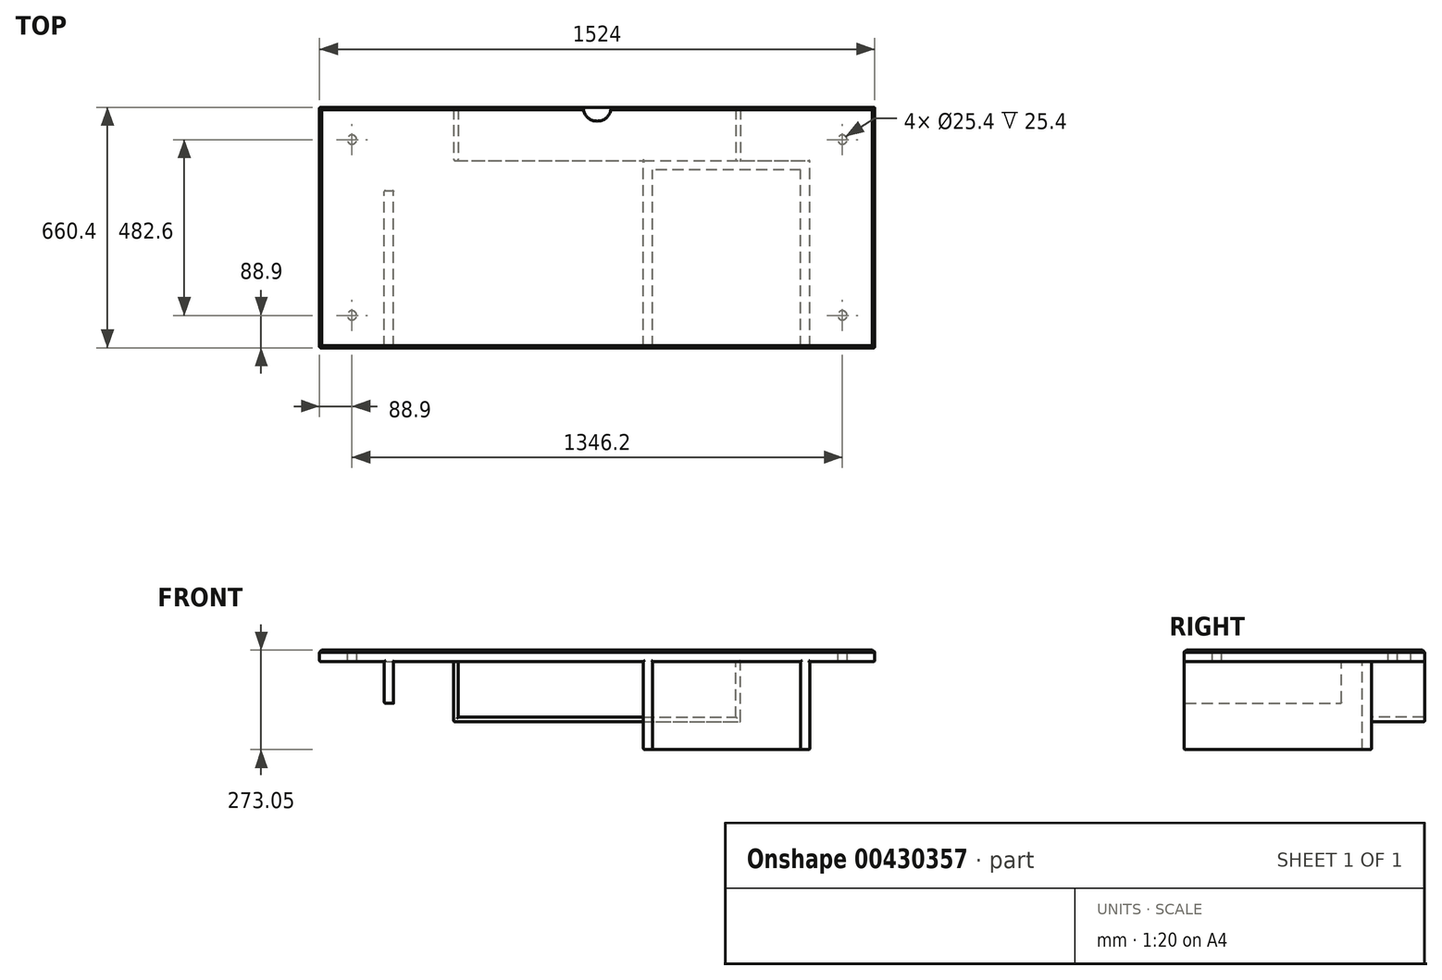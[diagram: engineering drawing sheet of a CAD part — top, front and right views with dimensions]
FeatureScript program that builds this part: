
annotation { "Feature Type Name" : "Feature", "Feature Type Description" : "" }
export const myFeature = defineFeature(function(context is Context, id is Id, definition is map)
    precondition{}
    {
        {
            var Q0;
            Q0=qCreatedBy(makeId("Top.planeOp"),FACE);
            var sketch = newSketch(context, id + "F0", { "sketchPlane" : qUnion([Q0])});
            skLineSegment(sketch, "E0.bottom", {"start": v(-762, 330.2) * mm, "end": v(762, 330.2) * mm});
            skLineSegment(sketch, "E0.top", {"start": v(-762, -330.2) * mm, "end": v(762, -330.2) * mm});
            skLineSegment(sketch, "E0.left", {"start": v(-762, 330.2) * mm, "end": v(-762, -330.2) * mm});
            skLineSegment(sketch, "E0.right", {"start": v(762, 330.2) * mm, "end": v(762, -330.2) * mm});
            skPoint(sketch, "E0.middle", {"position": v(0, 0) * mm});
            skSolve(sketch);
        }
        {
            var Q0;
            Q0=qSketchRegion(id+"F0",true);
            extrude(context, id + "F1", {"entities" : qUnion([Q0]), "oppositeDirection" : true, "depth" : 31.75 * mm});
        }
        {
            var Q0;
            Q0=makeQuery(id+"F1.opExtrude","CAP_FACE",FACE,{"disambiguationData":[OSD([sQuery(id+"F0.wireOp",EDGE,"E0.bottom"),sQuery(id+"F0.wireOp",EDGE,"E0.top"),sQuery(id+"F0.wireOp",EDGE,"E0.left"),sQuery(id+"F0.wireOp",EDGE,"E0.right")])],"isStart":true});
            var sketch = newSketch(context, id + "F2", { "sketchPlane" : qUnion([Q0])});
            skCircle(sketch, "E1", {"center": v(0, 330.2) * mm, "radius": 38.1 * mm});
            skSolve(sketch);
        }
        {
            var Q0;
            Q0=qSketchRegion(id+"F2",true);
            extrude(context, id + "F3", {"entities" : qUnion([Q0]), "operationType" : NewBodyOperationType.REMOVE, "endBound" : BoundingType.THROUGH_ALL, "oppositeDirection" : true, "depth" : 25.4 * mm});
        }
        {
            var Q0;
            Q0=makeQuery(id+"F1.opExtrude","CAP_FACE",FACE,{"disambiguationData":[OSD([sQuery(id+"F0.wireOp",EDGE,"E0.bottom"),sQuery(id+"F0.wireOp",EDGE,"E0.top"),sQuery(id+"F0.wireOp",EDGE,"E0.left"),sQuery(id+"F0.wireOp",EDGE,"E0.right")])],"isStart":false});
            var sketch = newSketch(context, id + "F4", { "sketchPlane" : qUnion([Q0])});
            skLineSegment(sketch, "E2.bottom", {"start": v(-584.2, 330.2) * mm, "end": v(-558.8, 330.2) * mm});
            skLineSegment(sketch, "E2.top", {"start": v(-584.2, -101.6) * mm, "end": v(-558.8, -101.6) * mm});
            skLineSegment(sketch, "E2.left", {"start": v(-584.2, 330.2) * mm, "end": v(-584.2, -101.6) * mm});
            skLineSegment(sketch, "E2.right", {"start": v(-558.8, 330.2) * mm, "end": v(-558.8, -101.6) * mm});
            skPoint(sketch, "E3.oppositeSnap0", {"position": v(-571.5, -101.6) * mm});
            skSolve(sketch);
        }
        {
            var Q0;
            Q0=qSketchRegion(id+"F4",true);
            extrude(context, id + "F5", {"entities" : qUnion([Q0]), "operationType" : NewBodyOperationType.ADD, "depth" : 114.3 * mm});
        }
        {
            var Q0;
            {var subQ0=sQuery(id+"F0.wireOp",EDGE,"E0.bottom");var subQ1=sQuery(id+"F0.wireOp",EDGE,"E0.right");Q0=makeQuery(id+"F3.boolean.opBoolean","SPLIT",EDGE,{"disambiguationData":[TD([makeQuery(id+"F1.opExtrude","SWEPT_FACE",FACE,{"disambiguationData":[OSD([subQ1])]})])],"derivedFrom":makeQuery(id+"F1.opExtrude","CAP_EDGE",EDGE,{"disambiguationData":[OSD([subQ0])],"isStart":true})});}
            var Q1;
            Q1=makeQuery(id+"F1.opExtrude","CAP_EDGE",EDGE,{"disambiguationData":[OSD([sQuery(id+"F0.wireOp",EDGE,"E0.right")])],"isStart":true});
            var Q2;
            {var subQ0=sQuery(id+"F0.wireOp",EDGE,"E0.bottom");var subQ1=sQuery(id+"F0.wireOp",EDGE,"E0.left");Q2=makeQuery(id+"F3.boolean.opBoolean","SPLIT",EDGE,{"disambiguationData":[TD([makeQuery(id+"F1.opExtrude","SWEPT_FACE",FACE,{"disambiguationData":[OSD([subQ1])]})])],"derivedFrom":makeQuery(id+"F1.opExtrude","CAP_EDGE",EDGE,{"disambiguationData":[OSD([subQ0])],"isStart":true})});}
            var Q3;
            Q3=makeQuery(id+"F1.opExtrude","CAP_EDGE",EDGE,{"disambiguationData":[OSD([sQuery(id+"F0.wireOp",EDGE,"E0.left")])],"isStart":true});
            var Q4;
            Q4=makeQuery(id+"F1.opExtrude","CAP_EDGE",EDGE,{"disambiguationData":[OSD([sQuery(id+"F0.wireOp",EDGE,"E0.top")])],"isStart":true});
            var Q5;
            Q5=makeQuery(id+"F3.boolean.opBoolean","COPY",EDGE,{"derivedFrom":makeQuery(id+"F3.opExtrude","CAP_EDGE",EDGE,{"disambiguationData":[OSD([sQuery(id+"F2.wireOp",EDGE,"E1")])],"isStart":true})});
            chamfer(context, id + "F6", {"entities" : qUnion([Q0, Q1, Q2, Q3, Q4, Q5]), "width" : 6.35 * mm, "tangentPropagation" : true});
        }
        {
            var Q0;
            Q0=makeQuery(id+"F1.opExtrude","CAP_FACE",FACE,{"disambiguationData":[OSD([sQuery(id+"F0.wireOp",EDGE,"E0.bottom"),sQuery(id+"F0.wireOp",EDGE,"E0.top"),sQuery(id+"F0.wireOp",EDGE,"E0.left"),sQuery(id+"F0.wireOp",EDGE,"E0.right")])],"isStart":false});
            var sketch = newSketch(context, id + "F7", { "sketchPlane" : qUnion([Q0])});
            skCircle(sketch, "E4", {"center": v(-673.1, 241.3) * mm, "radius": 12.7 * mm});
            skCircle(sketch, "E5", {"center": v(-673.1, -241.3) * mm, "radius": 12.7 * mm});
            skCircle(sketch, "E6", {"center": v(673.1, 241.3) * mm, "radius": 12.7 * mm});
            skCircle(sketch, "E7", {"center": v(673.1, -241.3) * mm, "radius": 12.7 * mm});
            skSolve(sketch);
        }
        {
            var Q0;
            Q0=qSketchRegion(id+"F7",true);
            extrude(context, id + "F8", {"entities" : qUnion([Q0]), "operationType" : NewBodyOperationType.REMOVE, "oppositeDirection" : true, "depth" : 25.4 * mm});
        }
        {
            var Q0;
            Q0=makeQuery(id+"F1.opExtrude","CAP_FACE",FACE,{"disambiguationData":[OSD([sQuery(id+"F0.wireOp",EDGE,"E0.bottom"),sQuery(id+"F0.wireOp",EDGE,"E0.top"),sQuery(id+"F0.wireOp",EDGE,"E0.left"),sQuery(id+"F0.wireOp",EDGE,"E0.right")])],"isStart":false});
            var sketch = newSketch(context, id + "F9", { "sketchPlane" : qUnion([Q0])});
            skLineSegment(sketch, "E8.bottom", {"start": v(127, 330.2) * mm, "end": v(152.4, 330.2) * mm});
            skLineSegment(sketch, "E8.top", {"start": v(127, -184.15) * mm, "end": v(152.4, -184.15) * mm});
            skLineSegment(sketch, "E8.left", {"start": v(127, 330.2) * mm, "end": v(127, -184.15) * mm});
            skLineSegment(sketch, "E8.right", {"start": v(152.4, 330.2) * mm, "end": v(152.4, -158.75) * mm});
            skLineSegment(sketch, "E9.bottom", {"start": v(558.8, 330.2) * mm, "end": v(584.2, 330.2) * mm});
            skLineSegment(sketch, "E9.top", {"start": v(558.8, -184.15) * mm, "end": v(584.2, -184.15) * mm});
            skLineSegment(sketch, "E9.left", {"start": v(558.8, 330.2) * mm, "end": v(558.8, -158.75) * mm});
            skLineSegment(sketch, "E9.right", {"start": v(584.2, 330.2) * mm, "end": v(584.2, -184.15) * mm});
            skLineSegment(sketch, "E10", {"start": v(584.2, -184.15) * mm, "end": v(127, -184.15) * mm});
            skLineSegment(sketch, "E11", {"start": v(558.8, -158.75) * mm, "end": v(152.4, -158.75) * mm});
            skSolve(sketch);
        }
        {
            var Q0;
            Q0=qSketchRegion(id+"F9",true);
            extrude(context, id + "F10", {"entities" : qUnion([Q0]), "operationType" : NewBodyOperationType.ADD, "depth" : 241.3 * mm});
        }
        {
            var Q0;
            {var subQ0=sQuery(id+"F0.wireOp",EDGE,"E0.bottom");var subQ1=sQuery(id+"F0.wireOp",EDGE,"E0.right");var subQ2=sQuery(id+"F0.wireOp",EDGE,"E0.top");var subQ3=sQuery(id+"F0.wireOp",EDGE,"E0.left");Q0=makeQuery(id+"F10.boolean.opBoolean","SPLIT",FACE,{"disambiguationData":[TD([makeQuery(id+"F1.opExtrude","SWEPT_FACE",FACE,{"disambiguationData":[OSD([subQ0])]})])],"derivedFrom":makeQuery(id+"F1.opExtrude","CAP_FACE",FACE,{"disambiguationData":[OSD([subQ0,subQ2,subQ3,subQ1])],"isStart":false})});}
            var sketch = newSketch(context, id + "F11", { "sketchPlane" : qUnion([Q0])});
            skLineSegment(sketch, "E12.bottom", {"start": v(-393.7, -330.2) * mm, "end": v(-381, -330.2) * mm});
            skLineSegment(sketch, "E12.top", {"start": v(-393.7, -184.15) * mm, "end": v(-381, -184.15) * mm});
            skLineSegment(sketch, "E12.left", {"start": v(-393.7, -330.2) * mm, "end": v(-393.7, -184.15) * mm});
            skLineSegment(sketch, "E12.right", {"start": v(-381, -330.2) * mm, "end": v(-381, -184.15) * mm});
            skLineSegment(sketch, "E13.bottom", {"start": v(393.7, -330.2) * mm, "end": v(381, -330.2) * mm});
            skLineSegment(sketch, "E13.top", {"start": v(393.7, -184.15) * mm, "end": v(381, -184.15) * mm});
            skLineSegment(sketch, "E13.left", {"start": v(393.7, -330.2) * mm, "end": v(393.7, -184.15) * mm});
            skLineSegment(sketch, "E13.right", {"start": v(381, -330.2) * mm, "end": v(381, -184.15) * mm});
            skLineSegment(sketch, "E14", {"start": v(-381, -330.2) * mm, "end": v(0, -330.2) * mm, "construction": true});
            skLineSegment(sketch, "E15", {"start": v(0, -330.2) * mm, "end": v(381, -330.2) * mm, "construction": true});
            skSolve(sketch);
        }
        {
            var Q0;
            Q0 = qSketchRegion(id + "F11", true);
            extrude(context, id + "F12", {"entities" : qUnion([Q0]), "operationType" : NewBodyOperationType.ADD, "depth" : 152.4 * mm});
        }
        {
            var Q0;
            Q0=makeQuery(id+"F12.opExtrude","CAP_FACE",FACE,{"disambiguationData":[OSD([sQuery(id+"F11.wireOp",EDGE,"E12.bottom"),sQuery(id+"F11.wireOp",EDGE,"E12.top"),sQuery(id+"F11.wireOp",EDGE,"E12.left"),sQuery(id+"F11.wireOp",EDGE,"E12.right")])],"isStart":false});
            var sketch = newSketch(context, id + "F13", { "sketchPlane" : qUnion([Q0])});
            skLineSegment(sketch, "E16.bottom", {"start": v(-393.7, -184.15) * mm, "end": v(393.7, -184.15) * mm});
            skLineSegment(sketch, "E16.top", {"start": v(-393.7, -330.2) * mm, "end": v(393.7, -330.2) * mm});
            skLineSegment(sketch, "E16.left", {"start": v(-393.7, -184.15) * mm, "end": v(-393.7, -330.2) * mm});
            skLineSegment(sketch, "E16.right", {"start": v(393.7, -184.15) * mm, "end": v(393.7, -330.2) * mm});
            skSolve(sketch);
        }
        {
            var Q0;
            Q0 = qSketchRegion(id + "F13", true);
            extrude(context, id + "F14", {"entities" : qUnion([Q0]), "operationType" : NewBodyOperationType.ADD, "depth" : 12.7 * mm});
        }
        {
            var Q0;
            {var subQ0=sQuery(id+"F0.wireOp",EDGE,"E0.left");var subQ1=sQuery(id+"F0.wireOp",EDGE,"E0.top");Q0=makeQuery(id+"F5.boolean.opBoolean","SPLIT",EDGE,{"disambiguationData":[TD([makeQuery(id+"F1.opExtrude","SWEPT_FACE",FACE,{"disambiguationData":[OSD([subQ0])]})])],"derivedFrom":makeQuery(id+"F1.opExtrude","CAP_EDGE",EDGE,{"disambiguationData":[OSD([subQ1])],"isStart":false})});}
            var Q1;
            {var subQ0=sQuery(id+"F0.wireOp",EDGE,"E0.bottom");var subQ1=sQuery(id+"F0.wireOp",EDGE,"E0.right");Q1=makeQuery(id+"F3.boolean.opBoolean","SPLIT",EDGE,{"disambiguationData":[TD([makeQuery(id+"F1.opExtrude","SWEPT_FACE",FACE,{"disambiguationData":[OSD([subQ1])]})])],"derivedFrom":makeQuery(id+"F1.opExtrude","CAP_EDGE",EDGE,{"disambiguationData":[OSD([subQ0])],"isStart":false})});}
            var Q2;
            {var subQ0=sQuery(id+"F0.wireOp",EDGE,"E0.bottom");var subQ1=sQuery(id+"F0.wireOp",EDGE,"E0.left");Q2=makeQuery(id+"F3.boolean.opBoolean","SPLIT",EDGE,{"disambiguationData":[TD([makeQuery(id+"F1.opExtrude","SWEPT_FACE",FACE,{"disambiguationData":[OSD([subQ1])]})])],"derivedFrom":makeQuery(id+"F1.opExtrude","CAP_EDGE",EDGE,{"disambiguationData":[OSD([subQ0])],"isStart":false})});}
            var Q3;
            Q3=makeQuery(id+"F1.opExtrude","CAP_EDGE",EDGE,{"disambiguationData":[OSD([sQuery(id+"F0.wireOp",EDGE,"E0.left")])],"isStart":false});
            var Q4;
            Q4=makeQuery(id+"F1.opExtrude","CAP_EDGE",EDGE,{"disambiguationData":[OSD([sQuery(id+"F0.wireOp",EDGE,"E0.right")])],"isStart":false});
            var Q5;
            Q5=makeQuery(id+"F5.opExtrude","SWEPT_EDGE",EDGE,{"disambiguationData":[OSD([sQuery(id+"F0.wireOp",EDGE,"E0.top"),sQuery(id+"F4.wireOp",EDGE,"E2.bottom"),sQuery(id+"F4.wireOp",EDGE,"E2.left")])]});
            var Q6;
            Q6=makeQuery(id+"F5.opExtrude","SWEPT_EDGE",EDGE,{"disambiguationData":[OSD([sQuery(id+"F0.wireOp",EDGE,"E0.top"),sQuery(id+"F4.wireOp",EDGE,"E2.bottom"),sQuery(id+"F4.wireOp",EDGE,"E2.right")])]});
            var Q7;
            Q7=makeQuery(id+"F5.opExtrude","CAP_EDGE",EDGE,{"disambiguationData":[OSD([sQuery(id+"F4.wireOp",EDGE,"E2.bottom")])],"isStart":false});
            var Q8;
            Q8=makeQuery(id+"F5.opExtrude","SWEPT_EDGE",EDGE,{"disambiguationData":[OSD([sQuery(id+"F0.wireOp",EDGE,"E0.top"),sQuery(id+"F4.wireOp",EDGE,"E2.bottom"),sQuery(id+"F4.wireOp",EDGE,"E2.left")])]});
            var Q9;
            Q9=makeQuery(id+"F5.opExtrude","SWEPT_EDGE",EDGE,{"disambiguationData":[OSD([sQuery(id+"F0.wireOp",EDGE,"E0.top"),sQuery(id+"F4.wireOp",EDGE,"E2.bottom"),sQuery(id+"F4.wireOp",EDGE,"E2.right")])]});
            var Q10;
            Q10=makeQuery(id+"F5.opExtrude","SWEPT_EDGE",EDGE,{"disambiguationData":[OSD([sQuery(id+"F0.wireOp",EDGE,"E0.top"),sQuery(id+"F4.wireOp",EDGE,"E2.bottom"),sQuery(id+"F4.wireOp",EDGE,"E2.left")])]});
            var Q11;
            Q11=makeQuery(id+"F5.opExtrude","SWEPT_EDGE",EDGE,{"disambiguationData":[OSD([sQuery(id+"F0.wireOp",EDGE,"E0.top"),sQuery(id+"F4.wireOp",EDGE,"E2.bottom"),sQuery(id+"F4.wireOp",EDGE,"E2.right")])]});
            var Q12;
            Q12=makeQuery(id+"F5.opExtrude","SWEPT_EDGE",EDGE,{"disambiguationData":[OSD([sQuery(id+"F4.wireOp",EDGE,"E2.top"),sQuery(id+"F4.wireOp",EDGE,"E2.left")])]});
            var Q13;
            Q13=makeQuery(id+"F5.opExtrude","SWEPT_EDGE",EDGE,{"disambiguationData":[OSD([sQuery(id+"F4.wireOp",EDGE,"E2.top"),sQuery(id+"F4.wireOp",EDGE,"E2.right")])]});
            var Q14;
            Q14=makeQuery(id+"F5.opExtrude","CAP_EDGE",EDGE,{"disambiguationData":[OSD([sQuery(id+"F4.wireOp",EDGE,"E2.top")])],"isStart":false});
            var Q15;
            Q15=makeQuery(id+"F5.opExtrude","CAP_EDGE",EDGE,{"disambiguationData":[OSD([sQuery(id+"F4.wireOp",EDGE,"E2.left")])],"isStart":false});
            var Q16;
            {var subQ0=sQuery(id+"F0.wireOp",EDGE,"E0.top");var subQ2=makeQuery(id+"F5.opExtrude","SWEPT_FACE",FACE,{"disambiguationData":[OSD([sQuery(id+"F4.wireOp",EDGE,"E2.right")])]});var subQ4=sQuery(id+"F0.wireOp",EDGE,"E0.right");Q16=makeQuery(id+"F10.boolean.opBoolean","SPLIT",EDGE,{"disambiguationData":[TD([subQ2])],"derivedFrom":makeQuery(id+"F5.boolean.opBoolean","SPLIT",EDGE,{"disambiguationData":[TD([makeQuery(id+"F1.opExtrude","SWEPT_FACE",FACE,{"disambiguationData":[OSD([subQ4])]})])],"derivedFrom":makeQuery(id+"F1.opExtrude","CAP_EDGE",EDGE,{"disambiguationData":[OSD([subQ0])],"isStart":false})})});}
            var Q17;
            Q17=makeQuery(id+"F10.opExtrude","SWEPT_EDGE",EDGE,{"disambiguationData":[OSD([sQuery(id+"F0.wireOp",EDGE,"E0.top"),sQuery(id+"F9.wireOp",EDGE,"E8.bottom"),sQuery(id+"F9.wireOp",EDGE,"E8.left")])]});
            var Q18;
            Q18=makeQuery(id+"F10.opExtrude","SWEPT_EDGE",EDGE,{"disambiguationData":[OSD([sQuery(id+"F0.wireOp",EDGE,"E0.top"),sQuery(id+"F9.wireOp",EDGE,"E8.bottom"),sQuery(id+"F9.wireOp",EDGE,"E8.right")])]});
            var Q19;
            {var subQ0=sQuery(id+"F0.wireOp",EDGE,"E0.top");var subQ3=sQuery(id+"F0.wireOp",EDGE,"E0.right");Q19=makeQuery(id+"F10.boolean.opBoolean","SPLIT",EDGE,{"disambiguationData":[TD([makeQuery(id+"F10.opExtrude","SWEPT_FACE",FACE,{"disambiguationData":[OSD([sQuery(id+"F9.wireOp",EDGE,"E8.right")])]})])],"derivedFrom":makeQuery(id+"F5.boolean.opBoolean","SPLIT",EDGE,{"disambiguationData":[TD([makeQuery(id+"F1.opExtrude","SWEPT_FACE",FACE,{"disambiguationData":[OSD([subQ3])]})])],"derivedFrom":makeQuery(id+"F1.opExtrude","CAP_EDGE",EDGE,{"disambiguationData":[OSD([subQ0])],"isStart":false})})});}
            var Q20;
            Q20=makeQuery(id+"F10.opExtrude","SWEPT_EDGE",EDGE,{"disambiguationData":[OSD([sQuery(id+"F0.wireOp",EDGE,"E0.top"),sQuery(id+"F9.wireOp",EDGE,"E9.bottom"),sQuery(id+"F9.wireOp",EDGE,"E9.left")])]});
            var Q21;
            Q21=makeQuery(id+"F10.opExtrude","SWEPT_EDGE",EDGE,{"disambiguationData":[OSD([sQuery(id+"F0.wireOp",EDGE,"E0.top"),sQuery(id+"F9.wireOp",EDGE,"E9.bottom"),sQuery(id+"F9.wireOp",EDGE,"E9.right")])]});
            var Q22;
            {var subQ0=sQuery(id+"F0.wireOp",EDGE,"E0.right");var subQ1=makeQuery(id+"F1.opExtrude","SWEPT_FACE",FACE,{"disambiguationData":[OSD([subQ0])]});var subQ2=sQuery(id+"F0.wireOp",EDGE,"E0.top");Q22=makeQuery(id+"F10.boolean.opBoolean","SPLIT",EDGE,{"disambiguationData":[TD([subQ1])],"derivedFrom":makeQuery(id+"F5.boolean.opBoolean","SPLIT",EDGE,{"disambiguationData":[TD([subQ1])],"derivedFrom":makeQuery(id+"F1.opExtrude","CAP_EDGE",EDGE,{"disambiguationData":[OSD([subQ2])],"isStart":false})})});}
            var Q23;
            Q23=makeQuery(id+"F1.opExtrude","SWEPT_EDGE",EDGE,{"disambiguationData":[OSD([sQuery(id+"F0.wireOp",EDGE,"E0.top"),sQuery(id+"F0.wireOp",EDGE,"E0.right")])]});
            var Q24;
            Q24=makeQuery(id+"F10.opExtrude","CAP_EDGE",EDGE,{"disambiguationData":[OSD([sQuery(id+"F9.wireOp",EDGE,"E8.bottom")])],"isStart":false});
            var Q25;
            Q25=makeQuery(id+"F10.opExtrude","CAP_EDGE",EDGE,{"disambiguationData":[OSD([sQuery(id+"F9.wireOp",EDGE,"E9.bottom")])],"isStart":false});
            var Q26;
            Q26=makeQuery(id+"F10.opExtrude","CAP_EDGE",EDGE,{"disambiguationData":[OSD([sQuery(id+"F9.wireOp",EDGE,"E9.right")])],"isStart":false});
            var Q27;
            Q27=makeQuery(id+"F10.opExtrude","CAP_EDGE",EDGE,{"disambiguationData":[OSD([sQuery(id+"F9.wireOp",EDGE,"E8.left")])],"isStart":false});
            var Q28;
            Q28=makeQuery(id+"F10.opExtrude","SWEPT_EDGE",EDGE,{"disambiguationData":[OSD([sQuery(id+"F9.wireOp",EDGE,"E9.right"),sQuery(id+"F9.wireOp",EDGE,"E10")])]});
            var Q29;
            Q29=makeQuery(id+"F10.opExtrude","CAP_EDGE",EDGE,{"disambiguationData":[OSD([sQuery(id+"F9.wireOp",EDGE,"E10")])],"isStart":false});
            var Q30;
            Q30=makeQuery(id+"F1.opExtrude","SWEPT_EDGE",EDGE,{"disambiguationData":[OSD([sQuery(id+"F0.wireOp",EDGE,"E0.bottom"),sQuery(id+"F0.wireOp",EDGE,"E0.right")])]});
            var Q31;
            Q31=makeQuery(id+"F14.boolean.opBoolean","MERGE",EDGE,{"derivedFrom":[makeQuery(id+"F12.opExtrude","SWEPT_EDGE",EDGE,{"disambiguationData":[OSD([sQuery(id+"F0.wireOp",EDGE,"E0.bottom"),sQuery(id+"F11.wireOp",EDGE,"E13.bottom"),sQuery(id+"F11.wireOp",EDGE,"E13.left")])]}),makeQuery(id+"F14.opExtrude","SWEPT_EDGE",EDGE,{"disambiguationData":[OSD([sQuery(id+"F13.wireOp",EDGE,"E16.top"),sQuery(id+"F13.wireOp",EDGE,"E16.right")])]})]});
            var Q32;
            Q32=makeQuery(id+"F12.opExtrude","SWEPT_EDGE",EDGE,{"disambiguationData":[OSD([sQuery(id+"F0.wireOp",EDGE,"E0.bottom"),sQuery(id+"F11.wireOp",EDGE,"E13.bottom"),sQuery(id+"F11.wireOp",EDGE,"E13.right")])]});
            var Q33;
            Q33=makeQuery(id+"F14.opExtrude","CAP_EDGE",EDGE,{"disambiguationData":[OSD([sQuery(id+"F13.wireOp",EDGE,"E16.top")])],"isStart":true});
            var Q34;
            Q34=makeQuery(id+"F14.opExtrude","CAP_EDGE",EDGE,{"disambiguationData":[OSD([sQuery(id+"F13.wireOp",EDGE,"E16.top")])],"isStart":false});
            var Q35;
            Q35=makeQuery(id+"F12.opExtrude","SWEPT_EDGE",EDGE,{"disambiguationData":[OSD([sQuery(id+"F0.wireOp",EDGE,"E0.bottom"),sQuery(id+"F11.wireOp",EDGE,"E12.bottom"),sQuery(id+"F11.wireOp",EDGE,"E12.right")])]});
            var Q36;
            Q36=makeQuery(id+"F14.boolean.opBoolean","MERGE",EDGE,{"derivedFrom":[makeQuery(id+"F12.opExtrude","SWEPT_EDGE",EDGE,{"disambiguationData":[OSD([sQuery(id+"F0.wireOp",EDGE,"E0.bottom"),sQuery(id+"F11.wireOp",EDGE,"E12.bottom"),sQuery(id+"F11.wireOp",EDGE,"E12.left")])]}),makeQuery(id+"F14.opExtrude","SWEPT_EDGE",EDGE,{"disambiguationData":[OSD([sQuery(id+"F13.wireOp",EDGE,"E16.top"),sQuery(id+"F13.wireOp",EDGE,"E16.left")])]})]});
            var Q37;
            Q37=makeQuery(id+"F14.opExtrude","CAP_EDGE",EDGE,{"disambiguationData":[OSD([sQuery(id+"F13.wireOp",EDGE,"E16.left")])],"isStart":false});
            var Q38;
            Q38=makeQuery(id+"F14.opExtrude","CAP_EDGE",EDGE,{"disambiguationData":[OSD([sQuery(id+"F13.wireOp",EDGE,"E16.right")])],"isStart":false});
            var Q39;
            Q39=makeQuery(id+"F12.opExtrude","SWEPT_EDGE",EDGE,{"disambiguationData":[OSD([sQuery(id+"F11.wireOp",EDGE,"E12.top"),sQuery(id+"F11.wireOp",EDGE,"E12.right")])]});
            var Q40;
            Q40=makeQuery(id+"F14.boolean.opBoolean","MERGE",EDGE,{"derivedFrom":[makeQuery(id+"F12.opExtrude","SWEPT_EDGE",EDGE,{"disambiguationData":[OSD([sQuery(id+"F11.wireOp",EDGE,"E12.top"),sQuery(id+"F11.wireOp",EDGE,"E12.left")])]}),makeQuery(id+"F14.opExtrude","SWEPT_EDGE",EDGE,{"disambiguationData":[OSD([sQuery(id+"F13.wireOp",EDGE,"E16.bottom"),sQuery(id+"F13.wireOp",EDGE,"E16.left")])]})]});
            var Q41;
            {var subQ0=sQuery(id+"F13.wireOp",EDGE,"E16.bottom");Q41=makeQuery(id+"F14.boolean.opBoolean","SPLIT",EDGE,{"disambiguationData":[topologyDisambiguationEdgeConnected([makeQuery(id+"F12.opExtrude","SWEPT_FACE",FACE,{"disambiguationData":[OSD([sQuery(id+"F11.wireOp",EDGE,"E12.top")])]})])],"derivedFrom":makeQuery(id+"F14.opExtrude","CAP_EDGE",EDGE,{"disambiguationData":[OSD([subQ0])],"isStart":true})});}
            var Q42;
            {var subQ0=sQuery(id+"F13.wireOp",EDGE,"E16.bottom");Q42=makeQuery(id+"F14.boolean.opBoolean","SPLIT",EDGE,{"disambiguationData":[topologyDisambiguationEdgeConnected([makeQuery(id+"F12.opExtrude","SWEPT_FACE",FACE,{"disambiguationData":[OSD([sQuery(id+"F11.wireOp",EDGE,"E12.top")])]})])],"derivedFrom":makeQuery(id+"F14.opExtrude","CAP_EDGE",EDGE,{"disambiguationData":[OSD([subQ0])],"isStart":false})});}
            var Q43;
            Q43=makeQuery(id+"F1.opExtrude","SWEPT_EDGE",EDGE,{"disambiguationData":[OSD([sQuery(id+"F0.wireOp",EDGE,"E0.bottom"),sQuery(id+"F0.wireOp",EDGE,"E0.left")])]});
            var Q44;
            Q44=makeQuery(id+"F1.opExtrude","SWEPT_EDGE",EDGE,{"disambiguationData":[OSD([sQuery(id+"F0.wireOp",EDGE,"E0.top"),sQuery(id+"F0.wireOp",EDGE,"E0.left")])]});
            var Q45;
            Q45=makeQuery(id+"F3.boolean.opBoolean","INTERSECT",EDGE,{"derivedFrom":[makeQuery(id+"F1.opExtrude","CAP_FACE",FACE,{"disambiguationData":[OSD([sQuery(id+"F0.wireOp",EDGE,"E0.bottom"),sQuery(id+"F0.wireOp",EDGE,"E0.top"),sQuery(id+"F0.wireOp",EDGE,"E0.left"),sQuery(id+"F0.wireOp",EDGE,"E0.right")])],"isStart":false}),makeQuery(id+"F3.opExtrude","SWEPT_FACE",FACE,{"disambiguationData":[OSD([sQuery(id+"F2.wireOp",EDGE,"E1")])]})]});
            var Q46;
            Q46=makeQuery(id+"F3.boolean.opBoolean","INTERSECT",EDGE,{"disambiguationData":[OD(1.0)],"derivedFrom":[makeQuery(id+"F1.opExtrude","SWEPT_FACE",FACE,{"disambiguationData":[OSD([sQuery(id+"F0.wireOp",EDGE,"E0.bottom")])]}),makeQuery(id+"F3.opExtrude","SWEPT_FACE",FACE,{"disambiguationData":[OSD([sQuery(id+"F2.wireOp",EDGE,"E1")])]})]});
            var Q47;
            Q47=makeQuery(id+"F3.boolean.opBoolean","INTERSECT",EDGE,{"disambiguationData":[OD(0.0)],"derivedFrom":[makeQuery(id+"F1.opExtrude","SWEPT_FACE",FACE,{"disambiguationData":[OSD([sQuery(id+"F0.wireOp",EDGE,"E0.bottom")])]}),makeQuery(id+"F3.opExtrude","SWEPT_FACE",FACE,{"disambiguationData":[OSD([sQuery(id+"F2.wireOp",EDGE,"E1")])]})]});
            fillet(context, id + "F15", {"entities" : qUnion([Q0, Q1, Q2, Q3, Q4, Q5, Q6, Q7, Q8, Q9, Q10, Q11, Q12, Q13, Q14, Q15, Q16, Q17, Q18, Q19, Q20, Q21, Q22, Q23, Q24, Q25, Q26, Q27, Q28, Q29, Q30, Q31, Q32, Q33, Q34, Q35, Q36, Q37, Q38, Q39, Q40, Q41, Q42, Q43, Q44, Q45, Q46, Q47]), "radius" : 3.17 * mm, "tangentPropagation" : true, "allowEdgeOverflow" : false});
        }
    });
